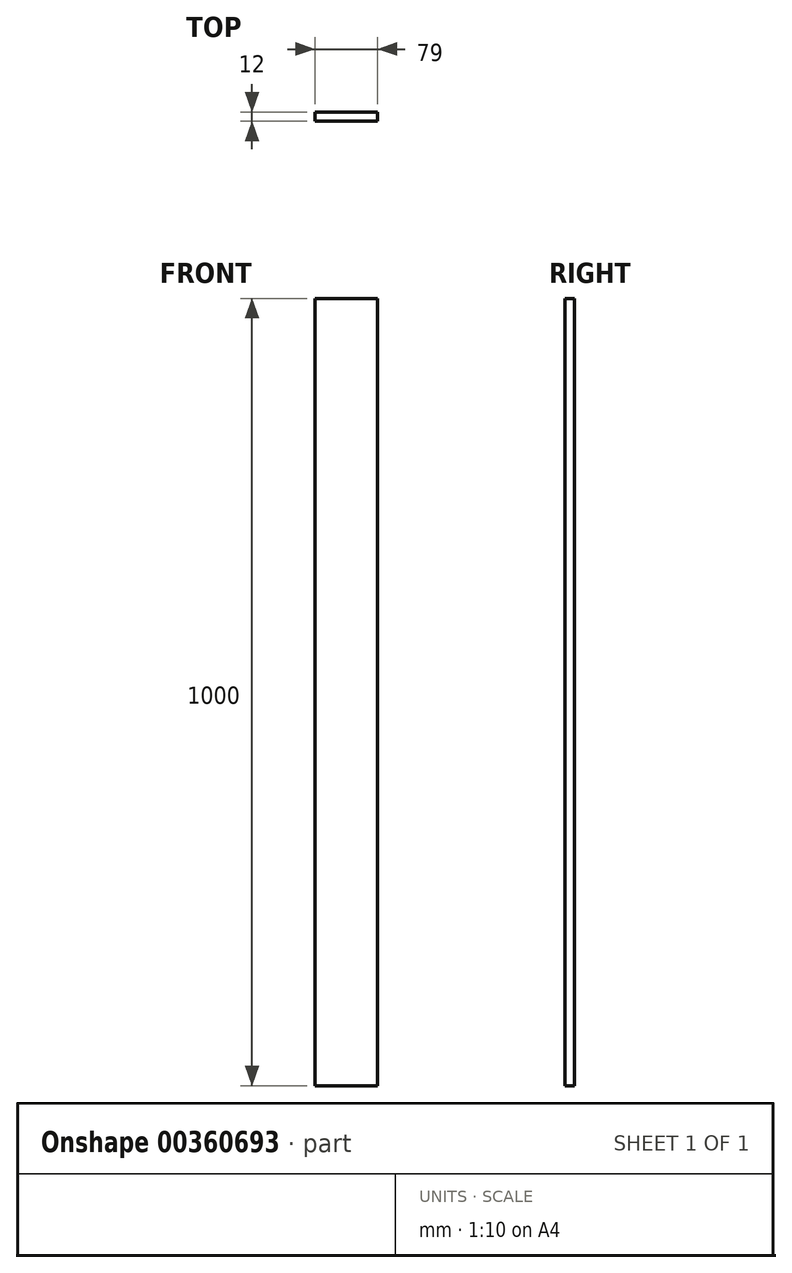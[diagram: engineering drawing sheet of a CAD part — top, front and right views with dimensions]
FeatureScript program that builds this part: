
annotation { "Feature Type Name" : "Feature", "Feature Type Description" : "" }
export const myFeature = defineFeature(function(context is Context, id is Id, definition is map)
    precondition{}
    {
        {
            var Q0;
            Q0=qCreatedBy(makeId("Front.planeOp"),FACE);
            var sketch = newSketch(context, id + "F0", { "sketchPlane" : qUnion([Q0])});
            skLineSegment(sketch, "E0.bottom", {"start": v(0, 0) * mm, "end": v(79, 0) * mm});
            skLineSegment(sketch, "E0.top", {"start": v(0, 1000) * mm, "end": v(79, 1000) * mm});
            skLineSegment(sketch, "E0.left", {"start": v(0, 0) * mm, "end": v(0, 1000) * mm});
            skLineSegment(sketch, "E0.right", {"start": v(79, 0) * mm, "end": v(79, 1000) * mm});
            skSolve(sketch);
        }
        {
            var Q0;
            Q0=makeQuery(id+"F0.imprint","IMPRINT",FACE,{"disambiguationData":[TD([[makeQuery(id+"F0.imprint","IMPRINT",EDGE,{"derivedFrom":sQuery(id+"F0.wireOp",EDGE,"E0.bottom")}),1.0]])]});
            extrude(context, id + "F1", {"entities" : qUnion([Q0]), "depth" : 12 * mm});
        }
    });
